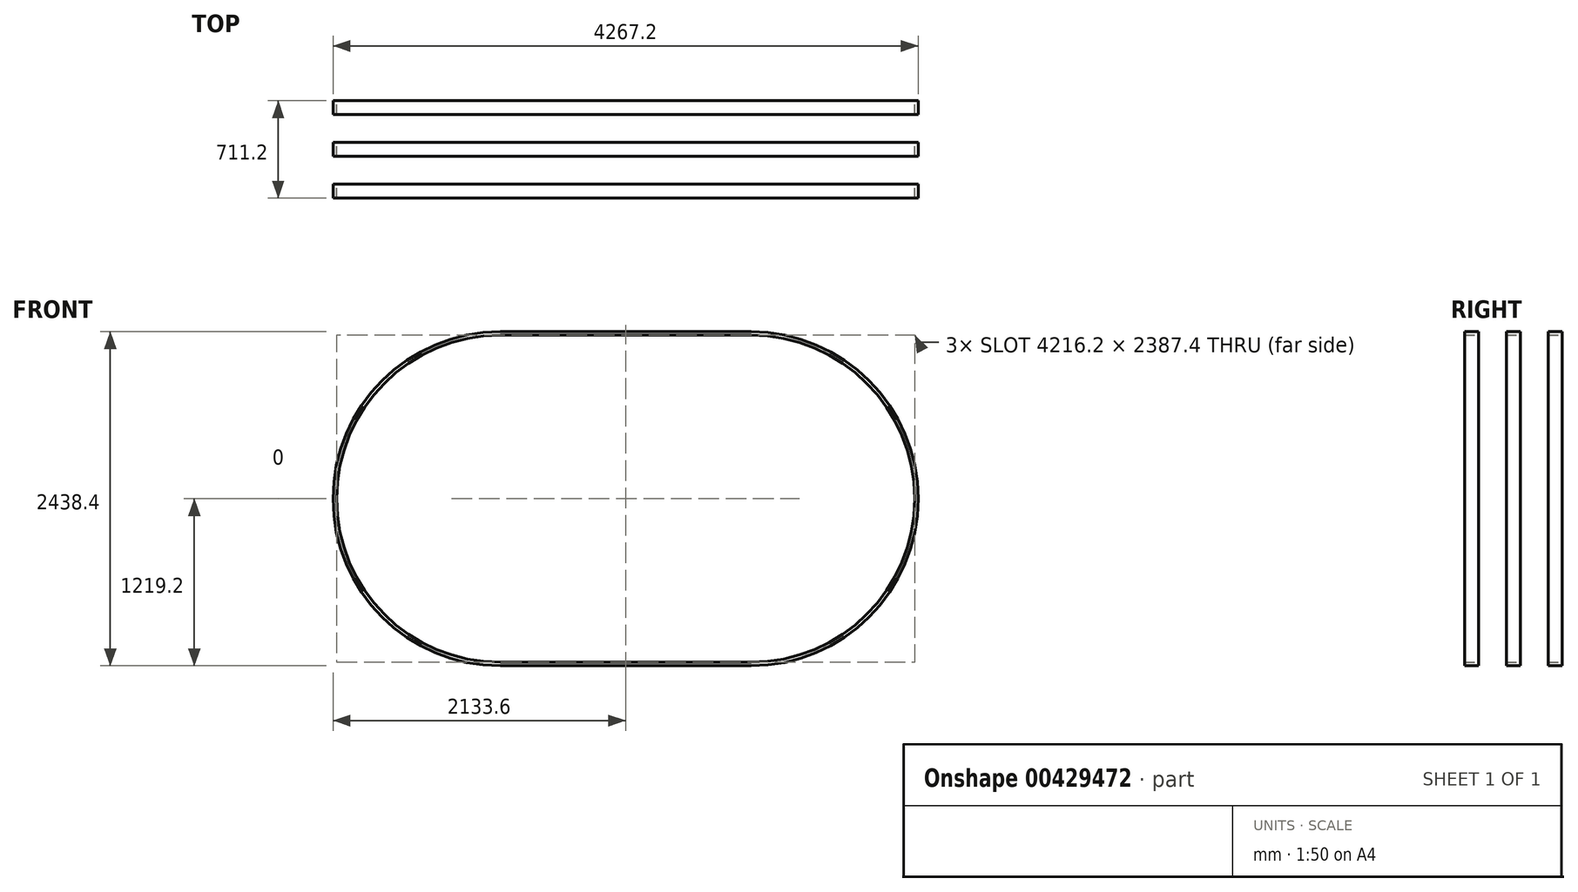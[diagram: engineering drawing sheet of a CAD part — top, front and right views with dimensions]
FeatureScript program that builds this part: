
annotation { "Feature Type Name" : "Feature", "Feature Type Description" : "" }
export const myFeature = defineFeature(function(context is Context, id is Id, definition is map)
    precondition{}
    {
        {
            var Q0;
            Q0=qCreatedBy(makeId("Front.planeOp"),FACE);
            var sketch = newSketch(context, id + "F0", { "sketchPlane" : qUnion([Q0])});
            skPoint(sketch, "E0.middle", {"position": v(0, 0) * mm});
            skArc(sketch, "E1", {"start": v(-914.4, 1219.2) * mm, "mid": v(-2133.6, 0) * mm, "end": v(-914.4, -1219.2) * mm});
            skLineSegment(sketch, "E2", {"start": v(-914.4, -1219.2) * mm, "end": v(914.4, -1219.2) * mm});
            skLineSegment(sketch, "E3", {"start": v(-914.4, 1219.2) * mm, "end": v(914.4, 1219.2) * mm});
            skArc(sketch, "E4.trimOffspring", {"start": v(914.4, -1219.2) * mm, "mid": v(2133.6, 0) * mm, "end": v(914.4, 1219.2) * mm});
            skPoint(sketch, "E5.start.orphan", {"position": v(-2133.6, 0) * mm});
            skLineSegment(sketch, "E6", {"start": v(0, 1219.2) * mm, "end": v(0, -1219.2) * mm, "construction": true});
            skLineSegment(sketch, "E7", {"start": v(-2133.6, 0) * mm, "end": v(2133.6, 0) * mm, "construction": true});
            skLineSegment(sketch, "E8", {"start": v(-914.4, 1219.2) * mm, "end": v(-914.4, -1219.2) * mm});
            skLineSegment(sketch, "E9", {"start": v(914.4, -1219.2) * mm, "end": v(914.4, 1219.2) * mm});
            skLineSegment(sketch, "E10", {"start": v(-914.4, 1193.7) * mm, "end": v(914.4, 1193.7) * mm});
            skLineSegment(sketch, "E11.MirrorCS", {"start": v(-914.4, -1193.7) * mm, "end": v(914.4, -1193.7) * mm});
            skArc(sketch, "E12", {"start": v(914.4, 1193.7) * mm, "mid": v(2108.1, 0) * mm, "end": v(914.4, -1193.7) * mm});
            skArc(sketch, "E13", {"start": v(-914.4, 1193.7) * mm, "mid": v(-2108.1, 0) * mm, "end": v(-914.4, -1193.7) * mm});
            skLineSegment(sketch, "E14", {"start": v(-2133.6, 0) * mm, "end": v(-2108.1, 0) * mm});
            skLineSegment(sketch, "E15", {"start": v(2133.6, 0) * mm, "end": v(2108.1, 0) * mm});
            skSolve(sketch);
        }
        {
            var Q0;
            {var subQ3=sQuery(id+"F0.wireOp",EDGE,"E14");Q0=makeQuery(id+"F0.imprint","IMPRINT",FACE,{"disambiguationData":[TD([[makeQuery(id+"F0.imprint","IMPRINT",EDGE,{"derivedFrom":subQ3}),-1.0]])]});}
            var Q1;
            {var subQ0=sQuery(id+"F0.wireOp",EDGE,"E2");Q1=makeQuery(id+"F0.imprint","IMPRINT",FACE,{"disambiguationData":[TD([[makeQuery(id+"F0.imprint","IMPRINT",EDGE,{"derivedFrom":subQ0}),1.0]])]});}
            var Q2;
            {var subQ3=sQuery(id+"F0.wireOp",EDGE,"E15");Q2=makeQuery(id+"F0.imprint","IMPRINT",FACE,{"disambiguationData":[TD([[makeQuery(id+"F0.imprint","IMPRINT",EDGE,{"derivedFrom":subQ3}),1.0]])]});}
            var Q3;
            {var subQ3=sQuery(id+"F0.wireOp",EDGE,"E14");Q3=makeQuery(id+"F0.imprint","IMPRINT",FACE,{"disambiguationData":[TD([[makeQuery(id+"F0.imprint","IMPRINT",EDGE,{"derivedFrom":subQ3}),1.0]])]});}
            var Q4;
            {var subQ3=sQuery(id+"F0.wireOp",EDGE,"E15");Q4=makeQuery(id+"F0.imprint","IMPRINT",FACE,{"disambiguationData":[TD([[makeQuery(id+"F0.imprint","IMPRINT",EDGE,{"derivedFrom":subQ3}),-1.0]])]});}
            var Q5;
            {var subQ0=sQuery(id+"F0.wireOp",EDGE,"E3");Q5=makeQuery(id+"F0.imprint","IMPRINT",FACE,{"disambiguationData":[TD([[makeQuery(id+"F0.imprint","IMPRINT",EDGE,{"derivedFrom":subQ0}),-1.0]])]});}
            extrude(context, id + "F1", {"entities" : qUnion([Q0, Q1, Q2, Q3, Q4, Q5]), "depth" : 101.6 * mm});
        }
        {
            var Q0;
            Q0=makeQuery(id+"F1.opExtrude","SWEPT_BODY",BODY,{"disambiguationData":[OSD([sQuery(id+"F0.wireOp",EDGE,"E1"),sQuery(id+"F0.wireOp",EDGE,"E2"),sQuery(id+"F0.wireOp",EDGE,"E3"),sQuery(id+"F0.wireOp",EDGE,"E4.trimOffspring"),sQuery(id+"F0.wireOp",EDGE,"E10"),sQuery(id+"F0.wireOp",EDGE,"E11.MirrorCS"),sQuery(id+"F0.wireOp",EDGE,"E12"),sQuery(id+"F0.wireOp",EDGE,"E13")])]});
            transform(context, id + "F2", {"entities" : qUnion([Q0]), "transformType" : TransformType.TRANSLATION_3D, "dx" : 0 * mm, "dy" : 304.8 * mm, "dz" : 0 * mm, "makeCopy" : true});
        }
        {
            var Q0;
            Q0=makeQuery(id+"F1.opExtrude","SWEPT_BODY",BODY,{"disambiguationData":[OSD([sQuery(id+"F0.wireOp",EDGE,"E1"),sQuery(id+"F0.wireOp",EDGE,"E2"),sQuery(id+"F0.wireOp",EDGE,"E3"),sQuery(id+"F0.wireOp",EDGE,"E4.trimOffspring"),sQuery(id+"F0.wireOp",EDGE,"E10"),sQuery(id+"F0.wireOp",EDGE,"E11.MirrorCS"),sQuery(id+"F0.wireOp",EDGE,"E12"),sQuery(id+"F0.wireOp",EDGE,"E13")])]});
            transform(context, id + "F3", {"entities" : qUnion([Q0]), "transformType" : TransformType.TRANSLATION_3D, "dx" : 0 * mm, "dy" : -304.8 * mm, "dz" : 0 * mm, "makeCopy" : true});
        }
    });
